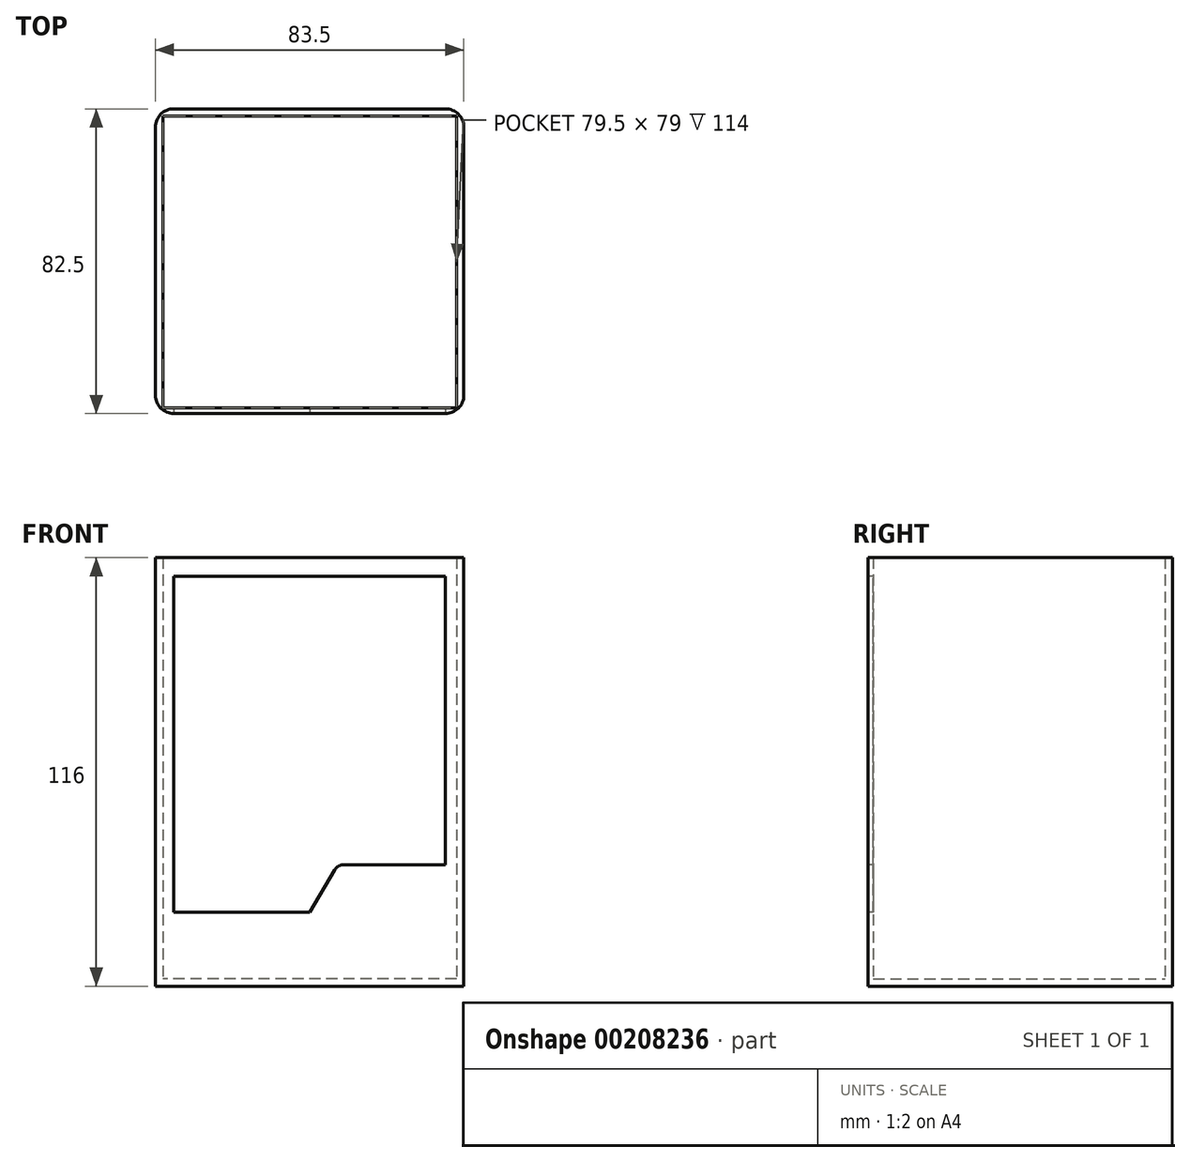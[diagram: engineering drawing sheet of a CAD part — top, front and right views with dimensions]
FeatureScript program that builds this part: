
annotation { "Feature Type Name" : "Feature", "Feature Type Description" : "" }
export const myFeature = defineFeature(function(context is Context, id is Id, definition is map)
    precondition{}
    {
        {
            var Q0;
            Q0=qCreatedBy(makeId("Top.planeOp"),FACE);
            var sketch = newSketch(context, id + "F0", { "sketchPlane" : qUnion([Q0])});
            skLineSegment(sketch, "E0.bottom", {"start": v(-83.5, 82.5) * mm, "end": v(0, 82.5) * mm});
            skLineSegment(sketch, "E0.top", {"start": v(-83.5, 0) * mm, "end": v(0, 0) * mm});
            skLineSegment(sketch, "E0.left", {"start": v(-83.5, 82.5) * mm, "end": v(-83.5, 0) * mm});
            skLineSegment(sketch, "E0.right", {"start": v(0, 82.5) * mm, "end": v(0, 0) * mm});
            skLineSegment(sketch, "E1", {"start": v(-43.8, 1.5) * mm, "end": v(-81.5, 1.5) * mm});
            skLineSegment(sketch, "E2", {"start": v(-81.5, 1.5) * mm, "end": v(-2, 1.5) * mm});
            skLineSegment(sketch, "E3", {"start": v(-2, 41.25) * mm, "end": v(-2, 80.5) * mm});
            skLineSegment(sketch, "E4", {"start": v(-2, 80.5) * mm, "end": v(-2, 1.5) * mm});
            skLineSegment(sketch, "E5", {"start": v(-41.75, 80.5) * mm, "end": v(-2, 80.5) * mm});
            skLineSegment(sketch, "E6", {"start": v(-2, 80.5) * mm, "end": v(-81.5, 80.5) * mm});
            skLineSegment(sketch, "E7", {"start": v(-81.5, 41.25) * mm, "end": v(-81.5, 80.5) * mm});
            skLineSegment(sketch, "E8", {"start": v(-81.5, 80.5) * mm, "end": v(-81.5, 1.5) * mm});
            skPoint(sketch, "E9.orphan", {"position": v(0, 80.5) * mm});
            skSolve(sketch);
        }
        {
            var Q0;
            Q0=makeQuery(id+"F0.imprint","IMPRINT",FACE,{"disambiguationData":[TD([[makeQuery(id+"F0.imprint","IMPRINT",EDGE,{"derivedFrom":sQuery(id+"F0.wireOp",EDGE,"E0.bottom")}),-1.0]])]});
            extrude(context, id + "F1", {"entities" : qUnion([Q0]), "depth" : 116 * mm});
        }
        {
            var Q0;
            Q0=qCreatedBy(makeId("Front.planeOp"),FACE);
            var sketch = newSketch(context, id + "F2", { "sketchPlane" : qUnion([Q0])});
            skLineSegment(sketch, "E10.bottom", {"start": v(-78.5, 111) * mm, "end": v(-5, 111) * mm});
            skLineSegment(sketch, "E10.top", {"start": v(-78.5, 20) * mm, "end": v(-41.75, 20) * mm});
            skLineSegment(sketch, "E10.left", {"start": v(-78.5, 111) * mm, "end": v(-78.5, 20) * mm});
            skLineSegment(sketch, "E10.right", {"start": v(-5, 111) * mm, "end": v(-5, 32.9) * mm});
            skPoint(sketch, "E11.start.orphan", {"position": v(-78.5, 65.5) * mm});
            skPoint(sketch, "E12.end.orphan", {"position": v(0, 65.5) * mm});
            skPoint(sketch, "E12.start.orphan", {"position": v(-5, 65.5) * mm});
            skPoint(sketch, "E13.start.orphan", {"position": v(-45.26, 0) * mm});
            skLineSegment(sketch, "E14", {"start": v(-34.12, 32.9) * mm, "end": v(-5, 32.9) * mm});
            skLineSegment(sketch, "E15", {"start": v(-41.75, 20) * mm, "end": v(-34.12, 32.9) * mm});
            skPoint(sketch, "E16.orphan", {"position": v(-5, 20) * mm});
            skSolve(sketch);
        }
        {
            var Q0;
            Q0 = qSketchRegion(id + "F2", true);
            extrude(context, id + "F3", {"entities" : qUnion([Q0]), "operationType" : NewBodyOperationType.REMOVE, "oppositeDirection" : true, "depth" : 25 * mm});
        }
        {
            var Q0;
            Q0=makeQuery(id+"F3.boolean.opBoolean","COPY",EDGE,{"derivedFrom":makeQuery(id+"F3.opExtrude","SWEPT_EDGE",EDGE,{"disambiguationData":[OSD([sQuery(id+"F2.wireOp",EDGE,"E14"),sQuery(id+"F2.wireOp",EDGE,"E15")])]})});
            fillet(context, id + "F4", {"entities" : qUnion([Q0]), "radius" : 3 * mm, "tangentPropagation" : true, "allowEdgeOverflow" : false});
        }
        {
            var Q0;
            {var subQ1=sQuery(id+"F0.wireOp",EDGE,"E2");var subQ6=makeQuery(id+"F0.imprint","IMPRINT",VERTEX,{"derivedFrom":subQ1});Q0=makeQuery(id+"F0.imprint","IMPRINT",FACE,{"disambiguationData":[TD([[makeQuery(id+"F0.imprint","IMPRINT",EDGE,{"disambiguationData":[TD([[subQ6,1.0]])],"derivedFrom":subQ1}),1.0]])]});}
            extrude(context, id + "F5", {"entities" : qUnion([Q0]), "operationType" : NewBodyOperationType.ADD, "depth" : 2 * mm});
        }
        {
            var Q0;
            Q0=makeQuery(id+"F1.opExtrude","SWEPT_EDGE",EDGE,{"disambiguationData":[OSD([sQuery(id+"F0.wireOp",EDGE,"E0.top"),sQuery(id+"F0.wireOp",EDGE,"E0.left")])]});
            var Q1;
            Q1=makeQuery(id+"F1.opExtrude","SWEPT_EDGE",EDGE,{"disambiguationData":[OSD([sQuery(id+"F0.wireOp",EDGE,"E0.top"),sQuery(id+"F0.wireOp",EDGE,"E0.right")])]});
            var Q2;
            Q2=makeQuery(id+"F1.opExtrude","SWEPT_EDGE",EDGE,{"disambiguationData":[OSD([sQuery(id+"F0.wireOp",EDGE,"E0.bottom"),sQuery(id+"F0.wireOp",EDGE,"E0.right")])]});
            var Q3;
            Q3=makeQuery(id+"F1.opExtrude","SWEPT_EDGE",EDGE,{"disambiguationData":[OSD([sQuery(id+"F0.wireOp",EDGE,"E0.bottom"),sQuery(id+"F0.wireOp",EDGE,"E0.left")])]});
            fillet(context, id + "F6", {"entities" : qUnion([Q0, Q1, Q2, Q3]), "radius" : 5 * mm, "tangentPropagation" : true, "allowEdgeOverflow" : false});
        }
    });
